# Revit family: QF_BOURGEAT_Etagères_Mobiles
name_source: partatom
category: Equipement spécialisé
revit_build: Autodesk Revit 2015 (Build: 20140606_1530(x64)
units: mm (PartAtom-declared; Revit-internal decimal feet)

## types (4) — shared parameters
Charge max = 300.00 kg
Fabricant = BOURGEAT
Hauteur hors tout = 1865 mm  [stored 6.11877 ft]
Spécification du Fabricant = Etagère mobile
URL catalogue = http://www.bourgeat.fr

## per-type parameters (varying)
| type | Longueur Clayette | Longueur Longeron | Longueur hors tout | Modèle | Profondeur hors tout | Type A |
| Etagère mobile 1100x435mm | 325 mm  [stored 1.06627 ft] | 980 mm  [stored 3.21522 ft] | 1100 mm | 819603 | 435 mm  [stored 1.42717 ft] | Oui |
| Etagère mobile 1100x610mm | 325 mm  [stored 1.06627 ft] | 980 mm  [stored 3.21522 ft] | 1100 mm | 819601 | 610 mm  [stored 2.00131 ft] | Oui |
| Etagère mobile 1425x610mm | 433 mm | 1305 mm  [stored 4.2815 ft] | 1425 mm  [stored 4.6752 ft] | 819801 | 610 mm  [stored 2.00131 ft] | Non |
| Etagère mobile 1425x435mm | 433 mm | 1305 mm  [stored 4.2815 ft] | 1425 mm  [stored 4.6752 ft] | 819803 | 435 mm  [stored 1.42717 ft] | Non |

note: [stored X ft] marks values corroborated as IEEE doubles in the binary element streams (Revit-internal decimal feet)
